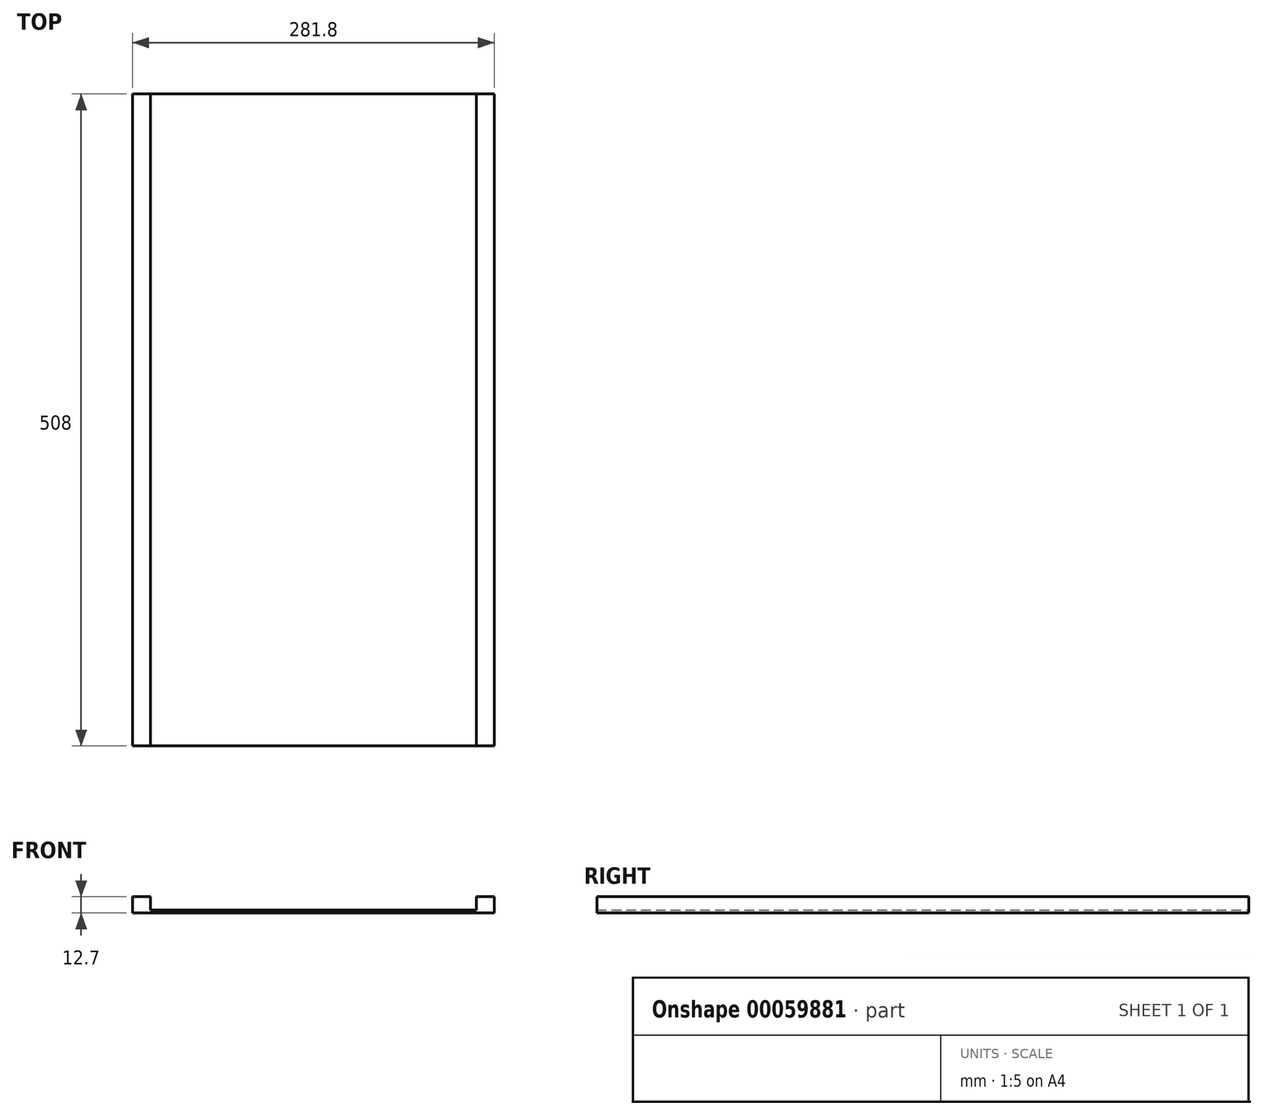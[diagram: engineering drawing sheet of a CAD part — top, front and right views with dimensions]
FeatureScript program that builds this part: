
annotation { "Feature Type Name" : "Feature", "Feature Type Description" : "" }
export const myFeature = defineFeature(function(context is Context, id is Id, definition is map)
    precondition{}
    {
        {
            var Q0;
            Q0=qCreatedBy(makeId("Front.planeOp"),FACE);
            var sketch = newSketch(context, id + "F0", { "sketchPlane" : qUnion([Q0])});
            skLineSegment(sketch, "E0.rect.bottom", {"start": v(127, -1.11) * mm, "end": v(-127, -1.11) * mm});
            skLineSegment(sketch, "E0.rect.top", {"start": v(127, 1.11) * mm, "end": v(-127, 1.11) * mm});
            skLineSegment(sketch, "E0.rect.left", {"start": v(127, -1.11) * mm, "end": v(127, 1.11) * mm});
            skLineSegment(sketch, "E0.rect.right", {"start": v(-127, -1.11) * mm, "end": v(-127, 1.11) * mm});
            skPoint(sketch, "E0.rect.middle", {"position": v(0, 0) * mm});
            skLineSegment(sketch, "E1", {"start": v(0, -39.17) * mm, "end": v(0, 35.66) * mm});
            skPoint(sketch, "E1.endSnap0", {"position": v(0, -1.11) * mm});
            skLineSegment(sketch, "E2.bottom", {"start": v(-140.9, 11.59) * mm, "end": v(-127, 11.59) * mm});
            skLineSegment(sketch, "E2.top", {"start": v(-140.9, -1.11) * mm, "end": v(-127, -1.11) * mm});
            skLineSegment(sketch, "E2.left", {"start": v(-140.9, 11.59) * mm, "end": v(-140.9, -1.11) * mm});
            skLineSegment(sketch, "E2.right", {"start": v(-127, 11.59) * mm, "end": v(-127, -1.11) * mm});
            skLineSegment(sketch, "E3.MirrorCS", {"start": v(127, 11.59) * mm, "end": v(127, -1.11) * mm});
            skLineSegment(sketch, "E4.MirrorCS", {"start": v(140.9, -1.11) * mm, "end": v(127, -1.11) * mm});
            skLineSegment(sketch, "E5.MirrorCS", {"start": v(140.9, 11.59) * mm, "end": v(140.9, -1.11) * mm});
            skLineSegment(sketch, "E6.MirrorCS", {"start": v(140.9, 11.59) * mm, "end": v(127, 11.59) * mm});
            skSolve(sketch);
        }
        {
            var Q0;
            Q0 = qSketchRegion(id + "F0", true);
            extrude(context, id + "F1", {"entities" : qUnion([Q0]), "depth" : 508 * mm});
        }
    });
